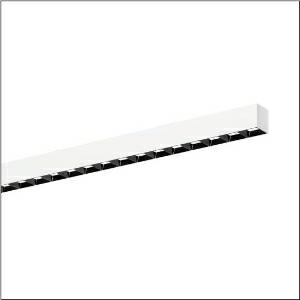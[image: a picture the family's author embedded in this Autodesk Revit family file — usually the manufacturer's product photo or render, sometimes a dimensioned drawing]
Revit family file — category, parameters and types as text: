
# Revit family: silica_21_51mx21tbt5w
name_source: partatom
category: Lighting Fixtures
units: mm (PartAtom-declared; Revit-internal decimal feet)

## family parameters
Cut with Voids When Loaded = No
Host = Face
Light Source = No
Part Type = Normal
Room Calculation Point = No
Round Connector Dimension = Use Diameter
Shared = No

## types (1)
- --- (1 x LED, 4650 lm, 40.3 W, 6500K)
    Apparent Load = 40 VA
    CIE Flux Codes = 85 99 100 100 100
    Color Rendering = 80
    Color Temperature = 6500K
    Default Elevation = 1800 mm
    Description = Silica 21, office luminaire, primary light control with darklight reflector, of PMMA, black, CAT 2 (L<= 3000cd/m²), light emission: direct distribution, primary light characteristic: symmetric, installation type: surface-mounted, LED, rated luminous flux: 4.650lm, luminous efficacy: 110lm/W, light colour: 8tw, colour temperature: 2700..6500K, control gear: DALI DT8, with terminal, 3+2-pole, max. 2.5mm², mains connection: 220..240V, AC, 50/60Hz, rated input power: 42.3W, luminaire housing, of aluminium, traffic white (RAL 9016), length: 1.504mm, width: 53mm, height: 53mm, protection rating (complete): IP20, insulation class (complete): insulation class I (protective earthing), certification: CE, permissible operating ambient temperature: 0..+35°C, standard: EN 50419, packaging unit: 1 piece
    Height = 53 mm
    Lamp = 1 x LED
    Lamp Light Flux = 4650 lm
    Lamp Power = 40.3 W
    Lamp count = 1
    Length = 1504 mm
    Luminous efficacy = 115 lm/W
    Manufacturer = Siteco
    ModVariant = No
    Model = 51MX21TBT5W
    Mounting Place = Ceiling
    Mounting Type = Surface mounted
    Number of Poles = 1
    OnlyDefault = Yes
    Power Factor = 1
    Product Name = Silica 21
    Product group = office luminaire | ceiling mounted
    ProductGroupID = 301
    Protection Class = Protection class I
    Protection Degree = IP 20
    RLX_Detail_Level = 1
    RLX_Emergency_Light_Flux = 0 lm
    RLX_Emergency_Type = 0
    RLX_Emergency_Type_DB = No
    RlxData = <blob elided: 41165 chars, md5=217c7810>
    Socket = socket
    Standby Power = 0 W
    System Light Flux = 4650 lm
    System Power = 40 W
    Type Comments = individual setting
    Type Image = l_1335873.jpg
    URL = http://relux.com
    VarID = @adj_139577
    Voltage = 0 V
    Weight = 0.00 kg
    Width = 53 mm

## geometry (parser evidence)
native form markers: Blend x4, Sweep x10
no freeform markers — native parametric forms only
